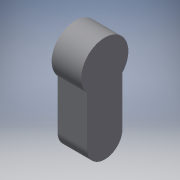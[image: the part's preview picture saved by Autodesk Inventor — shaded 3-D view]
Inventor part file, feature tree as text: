
AUTODESK INVENTOR PART (.ipt)
format: ipt  version: 2017 (Build 210142000, 142)  size: 100,352 bytes
history: native  units: in
note: dims shown in document units (in); Inventor stores cm internally (conversion verified against a paired STEP export)
features: extrude x1, sketch x1
ambient origin geometry x8: Origin, YZ Plane, XZ Plane, XY Plane, X Axis, Y Axis, Z Axis, Center Point
bodies: Solid1 (feature_tree)
feature tree (2):
  extrude  "Extrusion1"  Depth=1.18in
  sketch  "Sketch1"  dims[d0=1.57in d1=1.18in d2=3.52in d3=0.985in d4=0.0in]
